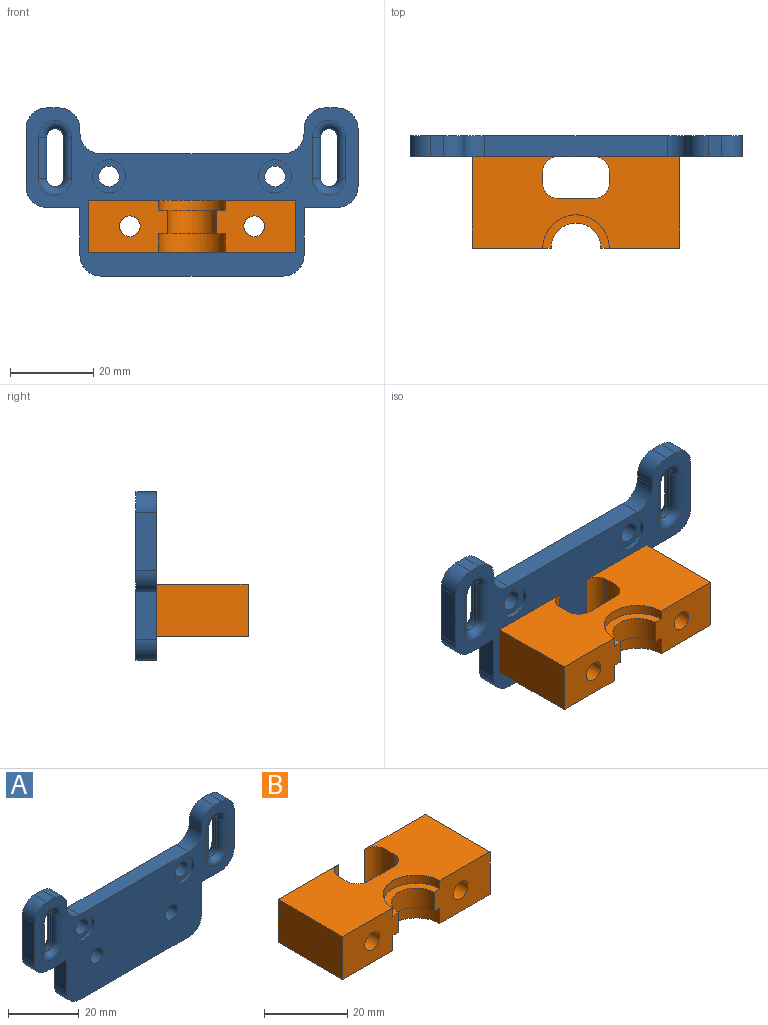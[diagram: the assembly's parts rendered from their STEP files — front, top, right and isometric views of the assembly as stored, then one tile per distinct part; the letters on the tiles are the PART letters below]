
ASSEMBLY  parts=2 mates=1
PART A: 70 faces, bbox 80x5x40.5 mm
  f0: plane 80x40.5mm, normal (0,1,0), area 1759.9mm2, adj f5,f6,f7,f8,f9,f10,f11,f12
  f1: plane 10x1mm, normal (1,0,0), area 10mm2, adj f44,f48,f49,f51
  f2: plane 10x1mm, normal (-1,0,0), area 10mm2, adj f42,f46,f48,f49
  f3: plane 10x1mm, normal (1,0,0), area 10mm2, adj f32,f34,f37,f40
  f4: plane 10x1mm, normal (-1,0,0), area 10mm2, adj f36,f37,f40,f41
  f5: plane 5x1mm, normal (1,0,0), area 5mm2, adj f0,f21,f22,f25
  f6: plane 5x3mm, normal (0,0,1), area 15mm2, adj f0,f21,f22,f23
  f7: plane 14x5mm, normal (-1,0,0), area 70mm2, adj f0,f21,f23,f24
  f8: plane 8x5mm, normal (0,0,-1), area 40mm2, adj f0,f9,f21,f24
  f9: plane 11.5x5mm, normal (-1,0,0), area 57.5mm2, adj f0,f8,f21,f27
  f10: plane 44x5mm, normal (0,0,-1), area 220mm2, adj f0,f21,f27,f28
  f11: plane 11.5x5mm, normal (1,0,0), area 57.5mm2, adj f0,f12,f21,f28
  f12: plane 8x5mm, normal (0,0,-1), area 40mm2, adj f0,f11,f21,f29
  f13: plane 14x5mm, normal (1,0,0), area 70mm2, adj f0,f21,f29,f30
  f14: plane 5x3mm, normal (0,0,1), area 15mm2, adj f0,f21,f30,f31
  f15: plane 5x1mm, normal (-1,0,0), area 5mm2, adj f0,f21,f26,f31
  f16: cylinder r=2.5mm len=5mm, axis (0,1,0), area 55mm2, adj f21,f58
  f17: cylinder r=4mm len=8mm, axis (0,1,0), area 25.1mm2, adj f21,f69
  f18: cylinder r=4mm len=8mm, axis (0,1,0), area 25.1mm2, adj f21,f67
  f19: plane 44x5mm, normal (0,0,1), area 220mm2, adj f0,f21,f25,f26
  f20: cylinder r=2.5mm len=5mm, axis (0,1,0), area 55mm2, adj f21,f65
  f21: plane 80x40.5mm, normal (0,-1,0), area 1784.5mm2, adj f5,f6,f7,f8,f9,f10,f11,f12
  f22: cylinder r=5mm len=5mm, axis (0,-1,0), area 39.3mm2, adj f0,f5,f6,f21
  f23: cylinder r=5mm len=5mm, axis (0,1,0), area 39.3mm2, adj f0,f6,f7,f21
  f24: cylinder r=5mm len=5mm, axis (0,-1,0), area 39.3mm2, adj f0,f7,f8,f21
  f25: cylinder r=5mm len=5mm, axis (0,1,0), area 39.3mm2, adj f0,f5,f19,f21
  f26: cylinder r=5mm len=5mm, axis (0,-1,0), area 39.3mm2, adj f0,f15,f19,f21
  f27: cylinder r=5mm len=5mm, axis (0,-1,0), area 39.3mm2, adj f0,f9,f10,f21
  f28: cylinder r=5mm len=5mm, axis (0,1,0), area 39.3mm2, adj f0,f10,f11,f21
  f29: cylinder r=5mm len=5mm, axis (0,-1,0), area 39.3mm2, adj f0,f12,f13,f21
  f30: cylinder r=5mm len=5mm, axis (0,1,0), area 39.3mm2, adj f0,f13,f14,f21
  f31: cylinder r=5mm len=5mm, axis (0,-1,0), area 39.3mm2, adj f0,f14,f15,f21
  f32: cylinder r=2mm len=10mm, axis (0,0,1), area 31.4mm2, adj f0,f3,f33,f35
  f33: torus R=4mm, axis (0,-1,0), area 26.9mm2, adj f0,f32,f36,f37
  f34: cylinder r=2mm len=10mm, axis (0,0,-1), area 31.4mm2, adj f3,f21,f38,f39
  f35: torus R=4mm, axis (0,-1,0), area 26.9mm2, adj f0,f32,f36,f40
  f36: cylinder r=2mm len=10mm, axis (0,0,-1), area 31.4mm2, adj f0,f4,f33,f35
  f37: cylinder r=2mm len=4mm, axis (0,-1,0), area 6.3mm2, adj f3,f4,f33,f38
  f38: torus R=4mm, axis (0,-1,0), area 26.9mm2, adj f21,f34,f37,f41
  f39: torus R=4mm, axis (0,-1,0), area 26.9mm2, adj f21,f34,f40,f41
  f40: cylinder r=2mm len=4mm, axis (0,1,0), area 6.3mm2, adj f3,f4,f35,f39
  f41: cylinder r=2mm len=10mm, axis (0,0,1), area 31.4mm2, adj f4,f21,f38,f39
  f42: cylinder r=2mm len=10mm, axis (0,0,-1), area 31.4mm2, adj f0,f2,f43,f45
  f43: torus R=4mm, axis (0,-1,0), area 26.9mm2, adj f0,f42,f44,f48
  f44: cylinder r=2mm len=10mm, axis (0,0,1), area 31.4mm2, adj f0,f1,f43,f45
  f45: torus R=4mm, axis (0,-1,0), area 26.9mm2, adj f0,f42,f44,f49
  f46: cylinder r=2mm len=10mm, axis (0,0,1), area 31.4mm2, adj f2,f21,f47,f50
  f47: torus R=4mm, axis (0,-1,0), area 26.9mm2, adj f21,f46,f48,f51
  f48: cylinder r=2mm len=4mm, axis (0,-1,0), area 6.3mm2, adj f1,f2,f43,f47
  f49: cylinder r=2mm len=4mm, axis (0,1,0), area 6.3mm2, adj f1,f2,f45,f50
  f50: torus R=4mm, axis (0,-1,0), area 26.9mm2, adj f21,f46,f49,f51
  f51: cylinder r=2mm len=10mm, axis (0,0,-1), area 31.4mm2, adj f1,f21,f47,f50
  f52: plane 4.63x1.62mm, normal (-0.33,0,-0.94), area 7.4mm2, adj f0,f53,f57,f58
  f53: plane 3.72x3.21mm, normal (0.65,0,-0.76), area 7.4mm2, adj f0,f52,f54,f58
  f54: plane 4.82x1.5mm, normal (0.98,0,0.19), area 7.4mm2, adj f0,f53,f55,f58
  f55: plane 4.63x1.62mm, normal (0.33,0,0.94), area 7.4mm2, adj f0,f54,f56,f58
  f56: plane 3.72x3.21mm, normal (-0.65,0,0.76), area 7.4mm2, adj f0,f55,f57,f58
  f57: plane 4.82x1.5mm, normal (-0.98,0,-0.19), area 7.4mm2, adj f0,f52,f56,f58
  f58: plane 9.64x9.27mm, normal (0,1,0), area 42.9mm2, adj f16,f52,f53,f54,f55,f56,f57
  f59: plane 4.63x1.62mm, normal (-0.33,0,0.94), area 7.4mm2, adj f0,f60,f64,f65
  f60: plane 4.82x1.5mm, normal (-0.98,0,0.19), area 7.4mm2, adj f0,f59,f61,f65
  f61: plane 3.72x3.21mm, normal (-0.65,0,-0.76), area 7.4mm2, adj f0,f60,f62,f65
  f62: plane 4.63x1.62mm, normal (0.33,0,-0.94), area 7.4mm2, adj f0,f61,f63,f65
  f63: plane 4.82x1.5mm, normal (0.98,0,-0.19), area 7.4mm2, adj f0,f62,f64,f65
  f64: plane 3.72x3.21mm, normal (0.65,0,0.76), area 7.4mm2, adj f0,f59,f63,f65
  f65: plane 9.64x9.27mm, normal (0,1,0), area 42.9mm2, adj f20,f59,f60,f61,f62,f63,f64
  f66: cylinder r=2.5mm len=5mm, axis (0,1,0), area 62.8mm2, adj f0,f67
  f67: plane 8x8mm, normal (0,-1,0), area 30.6mm2, adj f18,f66
  f68: cylinder r=2.5mm len=5mm, axis (0,1,0), area 62.8mm2, adj f0,f69
  f69: plane 8x8mm, normal (0,-1,0), area 30.6mm2, adj f17,f68
PART B: 22 faces, bbox 50x22x12.6 mm
  f0: cylinder r=8mm len=16mm, axis (0,0,-1), area 113.1mm2, adj f5,f8,f20,f21
  f1: plane 22x12.6mm, normal (-1,0,0), area 277.2mm2, adj f4,f5,f19,f20
  f2: plane 22x12.6mm, normal (1,0,0), area 277.2mm2, adj f4,f5,f11,f21
  f3: cylinder r=8mm len=16mm, axis (0,0,-1), area 60.3mm2, adj f4,f7,f20,f21
  f4: plane 50x22mm, normal (0,0,1), area 850mm2, adj f1,f2,f3,f11,f12,f13,f14,f15
  f5: plane 50x22mm, normal (0,0,-1), area 850mm2, adj f0,f1,f2,f11,f12,f13,f14,f15
  f6: cylinder r=6mm len=12mm, axis (0,0,-1), area 107.4mm2, adj f7,f8,f20,f21
  f7: plane 16x8mm, normal (0,0,1), area 44mm2, adj f3,f6,f20,f21
  f8: plane 16x8mm, normal (0,0,-1), area 44mm2, adj f0,f6,f20,f21
  f9: cylinder r=2.5mm len=22mm, axis (0,-1,0), area 345.6mm2, adj f11,f21
  f10: cylinder r=2.5mm len=22mm, axis (0,-1,0), area 345.6mm2, adj f19,f20
  f11: plane 20.5x12.6mm, normal (0,1,0), area 238.7mm2, adj f2,f4,f5,f9,f12
  f12: cylinder r=3.5mm len=12.6mm, axis (0,0,-1), area 69.3mm2, adj f4,f5,f11,f13
  f13: plane 12.6x3mm, normal (-1,0,0), area 37.8mm2, adj f4,f5,f12,f14
  f14: cylinder r=3.5mm len=12.6mm, axis (0,0,-1), area 69.3mm2, adj f4,f5,f13,f15
  f15: plane 12.6x9mm, normal (0,1,0), area 113.4mm2, adj f4,f5,f14,f16
  f16: cylinder r=3.5mm len=12.6mm, axis (0,0,-1), area 69.3mm2, adj f4,f5,f15,f17
  f17: plane 12.6x3mm, normal (1,0,0), area 37.8mm2, adj f4,f5,f16,f18
  f18: cylinder r=3.5mm len=12.6mm, axis (0,0,-1), area 69.3mm2, adj f4,f5,f17,f19
  f19: plane 20.5x12.6mm, normal (0,1,0), area 238.7mm2, adj f1,f4,f5,f10,f18
  f20: plane 19x12.6mm, normal (0,-1,0), area 206mm2, adj f0,f1,f3,f4,f5,f6,f7,f8
  f21: plane 19x12.6mm, normal (0,-1,0), area 206mm2, adj f0,f2,f3,f4,f5,f6,f7,f8
PLACE A t=(-3.66,10.56,8.03)mm
PLACE B t=(-3.66,-16.44,-1.02)mm
MATE planar B.f9 <-> A.f16  axis (0,1,0) through (11.34,5.56,5.28)mm
